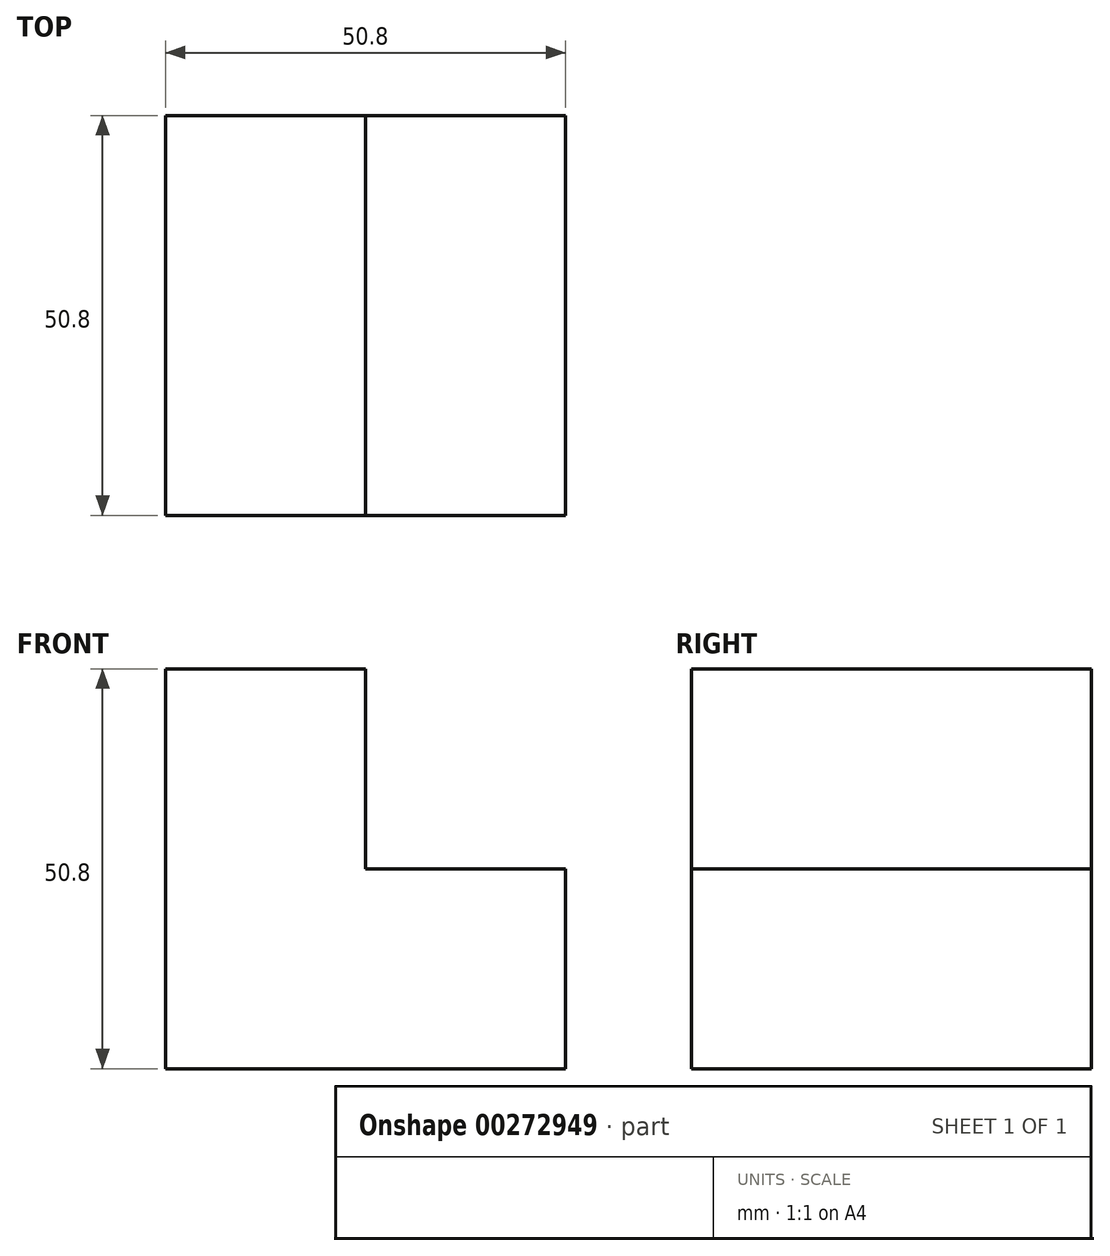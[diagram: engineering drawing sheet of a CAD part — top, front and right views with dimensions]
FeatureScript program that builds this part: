
annotation { "Feature Type Name" : "Feature", "Feature Type Description" : "" }
export const myFeature = defineFeature(function(context is Context, id is Id, definition is map)
    precondition{}
    {
        {
            var Q0;
            Q0=qCreatedBy(makeId("Front.planeOp"),FACE);
            var sketch = newSketch(context, id + "F0", { "sketchPlane" : qUnion([Q0])});
            skLineSegment(sketch, "E0", {"start": v(0, 0) * mm, "end": v(-50.8, 0) * mm});
            skLineSegment(sketch, "E1", {"start": v(-50.8, 0) * mm, "end": v(-50.8, 50.8) * mm});
            skLineSegment(sketch, "E2", {"start": v(-50.8, 50.8) * mm, "end": v(-25.4, 50.8) * mm});
            skLineSegment(sketch, "E3", {"start": v(-25.4, 50.8) * mm, "end": v(-25.4, 50.8) * mm});
            skLineSegment(sketch, "E4", {"start": v(-25.4, 25.4) * mm, "end": v(-25.4, 50.8) * mm});
            skLineSegment(sketch, "E5", {"start": v(-25.4, 25.4) * mm, "end": v(0, 25.4) * mm});
            skLineSegment(sketch, "E6", {"start": v(0, 25.4) * mm, "end": v(0, 0) * mm});
            skSolve(sketch);
        }
        {
            var Q0;
            Q0 = qSketchRegion(id + "F0", true);
            extrude(context, id + "F1", {"entities" : qUnion([Q0]), "depth" : 50.8 * mm});
        }
    });
